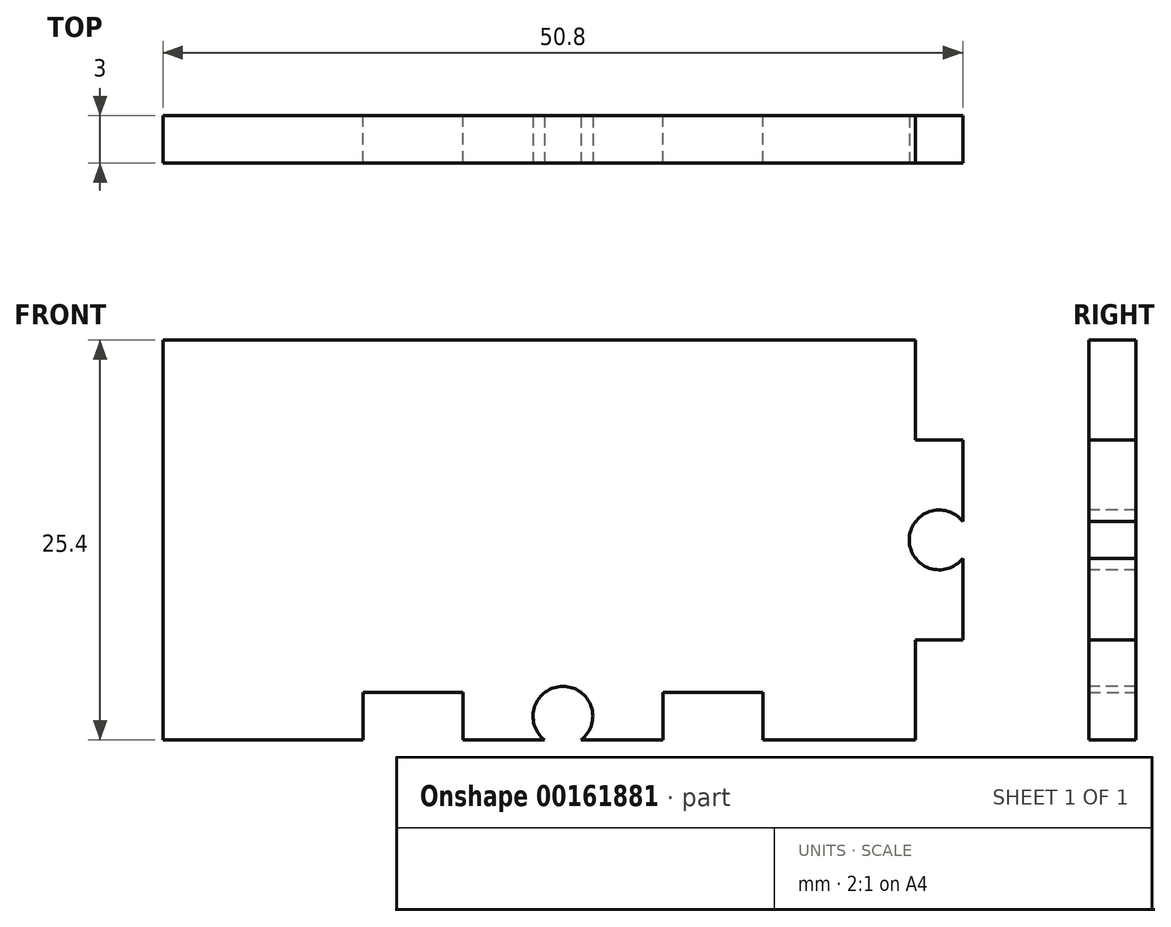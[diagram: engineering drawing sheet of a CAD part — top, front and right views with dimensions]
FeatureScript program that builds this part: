
annotation { "Feature Type Name" : "Feature", "Feature Type Description" : "" }
export const myFeature = defineFeature(function(context is Context, id is Id, definition is map)
    precondition{}
    {
        {
            var Q0;
            Q0=qCreatedBy(makeId("Front.planeOp"),FACE);
            var sketch = newSketch(context, id + "F0", { "sketchPlane" : qUnion([Q0])});
            skLineSegment(sketch, "E0.bottom", {"start": v(-25.4, 12.7) * mm, "end": v(22.4, 12.7) * mm});
            skLineSegment(sketch, "E0.top", {"start": v(-25.4, -12.7) * mm, "end": v(-12.7, -12.7) * mm});
            skLineSegment(sketch, "E0.left", {"start": v(-25.4, 12.7) * mm, "end": v(-25.4, -12.7) * mm});
            skLineSegment(sketch, "E0.right", {"start": v(25.4, 6.35) * mm, "end": v(25.4, -6.35) * mm});
            skPoint(sketch, "E0.middle", {"position": v(0, 0) * mm});
            skLineSegment(sketch, "E1.0", {"start": v(-12.7, -9.7) * mm, "end": v(-6.35, -9.7) * mm});
            skLineSegment(sketch, "E2.0", {"start": v(-6.35, -9.7) * mm, "end": v(-6.35, -12.7) * mm});
            skLineSegment(sketch, "E3.0", {"start": v(6.35, -9.7) * mm, "end": v(6.35, -12.7) * mm});
            skLineSegment(sketch, "E4.0", {"start": v(12.7, -9.7) * mm, "end": v(12.7, -12.7) * mm});
            skLineSegment(sketch, "E5.0", {"start": v(-12.7, -9.7) * mm, "end": v(-12.7, -12.7) * mm});
            skLineSegment(sketch, "E6.trimOffspring", {"start": v(-6.35, -12.7) * mm, "end": v(6.35, -12.7) * mm});
            skLineSegment(sketch, "E7.trimOffspring", {"start": v(12.7, -12.7) * mm, "end": v(22.4, -12.7) * mm});
            skLineSegment(sketch, "E8.trimOffspring", {"start": v(6.35, -9.7) * mm, "end": v(12.7, -9.7) * mm});
            skLineSegment(sketch, "E9", {"start": v(25.4, -6.35) * mm, "end": v(22.4, -6.35) * mm});
            skLineSegment(sketch, "E10", {"start": v(22.4, -6.35) * mm, "end": v(22.4, -12.7) * mm});
            skLineSegment(sketch, "E11", {"start": v(25.4, 6.35) * mm, "end": v(22.4, 6.35) * mm});
            skLineSegment(sketch, "E12", {"start": v(22.4, 6.35) * mm, "end": v(22.4, 12.7) * mm});
            skPoint(sketch, "E13.orphan", {"position": v(25.4, 12.7) * mm});
            skSolve(sketch);
        }
        {
            var Q0;
            Q0 = qSketchRegion(id + "F0", true);
            extrude(context, id + "F1", {"entities" : qUnion([Q0]), "depth" : 3 * mm});
        }
        {
            var Q0;
            Q0=makeQuery(id+"F1.opExtrude","CAP_FACE",FACE,{"disambiguationData":[OSD([sQuery(id+"F0.wireOp",EDGE,"E0.bottom"),sQuery(id+"F0.wireOp",EDGE,"E0.top"),sQuery(id+"F0.wireOp",EDGE,"E0.left"),sQuery(id+"F0.wireOp",EDGE,"E0.right")])],"isStart":false});
            var sketch = newSketch(context, id + "F2", { "sketchPlane" : qUnion([Q0])});
            skLineSegment(sketch, "E14.0", {"start": v(-25.4, -12.7) * mm, "end": v(-25.4, -12.7) * mm});
            skLineSegment(sketch, "E15.0", {"start": v(-25.4, -11.2) * mm, "end": v(25.4, -11.2) * mm, "construction": true});
            skPoint(sketch, "E16", {"position": v(0, -11.2) * mm});
            skPoint(sketch, "E17", {"position": v(-113.52, -14.29) * mm});
            skLineSegment(sketch, "E18.0", {"start": v(23.9, 6.35) * mm, "end": v(23.9, -6.35) * mm, "construction": true});
            skPoint(sketch, "E19", {"position": v(23.9, 0) * mm});
            skSolve(sketch);
        }
        {
            var Q0;
            Q0=sQuery(id+"F2.wireOp",VERTEX,"E16");
            var Q1;
            Q1=makeQuery(id+"F1.opExtrude","SWEPT_BODY",BODY,{"disambiguationData":[OSD([sQuery(id+"F0.wireOp",EDGE,"E0.bottom"),sQuery(id+"F0.wireOp",EDGE,"E0.top"),sQuery(id+"F0.wireOp",EDGE,"E0.left"),sQuery(id+"F0.wireOp",EDGE,"E0.right")])]});
            hole(context, id + "F3", {"style" : HoleStyle.SIMPLE, "endStyle" : HoleEndStyle.THROUGH, "standardTappedOrClearance" : lookupTablePath({ "standard" : "ANSI", "fit" : "Normal (ASME)", "size" : "#6", "type" : "Clearance" }), "standardBlindInLast" : lookupTablePath({ "fit" : "Free", "standard" : "ANSI", "size" : "#6", "type" : "Clearance" }), "holeDiameter" : 3.8 * mm, "locations" : qUnion([Q0]), "scope" : qUnion([Q1]), "isTappedThrough" : true});
        }
        {
            var Q0;
            Q0=sQuery(id+"F2.wireOp",VERTEX,"E19");
            var Q1;
            Q1=makeQuery(id+"F1.opExtrude","SWEPT_BODY",BODY,{"disambiguationData":[OSD([sQuery(id+"F0.wireOp",EDGE,"E0.bottom"),sQuery(id+"F0.wireOp",EDGE,"E0.top"),sQuery(id+"F0.wireOp",EDGE,"E0.left"),sQuery(id+"F0.wireOp",EDGE,"E0.right"),sQuery(id+"F0.wireOp",EDGE,"E1.0"),sQuery(id+"F0.wireOp",EDGE,"E2.0"),sQuery(id+"F0.wireOp",EDGE,"E3.0"),sQuery(id+"F0.wireOp",EDGE,"E4.0"),sQuery(id+"F0.wireOp",EDGE,"E5.0"),sQuery(id+"F0.wireOp",EDGE,"E6.trimOffspring"),sQuery(id+"F0.wireOp",EDGE,"E7.trimOffspring"),sQuery(id+"F0.wireOp",EDGE,"E8.trimOffspring"),sQuery(id+"F0.wireOp",EDGE,"E9"),sQuery(id+"F0.wireOp",EDGE,"E10"),sQuery(id+"F0.wireOp",EDGE,"E11"),sQuery(id+"F0.wireOp",EDGE,"E12")])]});
            hole(context, id + "F4", {"style" : HoleStyle.SIMPLE, "endStyle" : HoleEndStyle.THROUGH, "standardTappedOrClearance" : lookupTablePath({ "standard" : "ANSI", "fit" : "Normal (ASME)", "size" : "#6", "type" : "Clearance" }), "standardBlindInLast" : lookupTablePath({ "fit" : "Free", "standard" : "ANSI", "size" : "#6", "type" : "Clearance" }), "holeDiameter" : 3.8 * mm, "locations" : qUnion([Q0]), "scope" : qUnion([Q1]), "isTappedThrough" : true});
        }
    });
